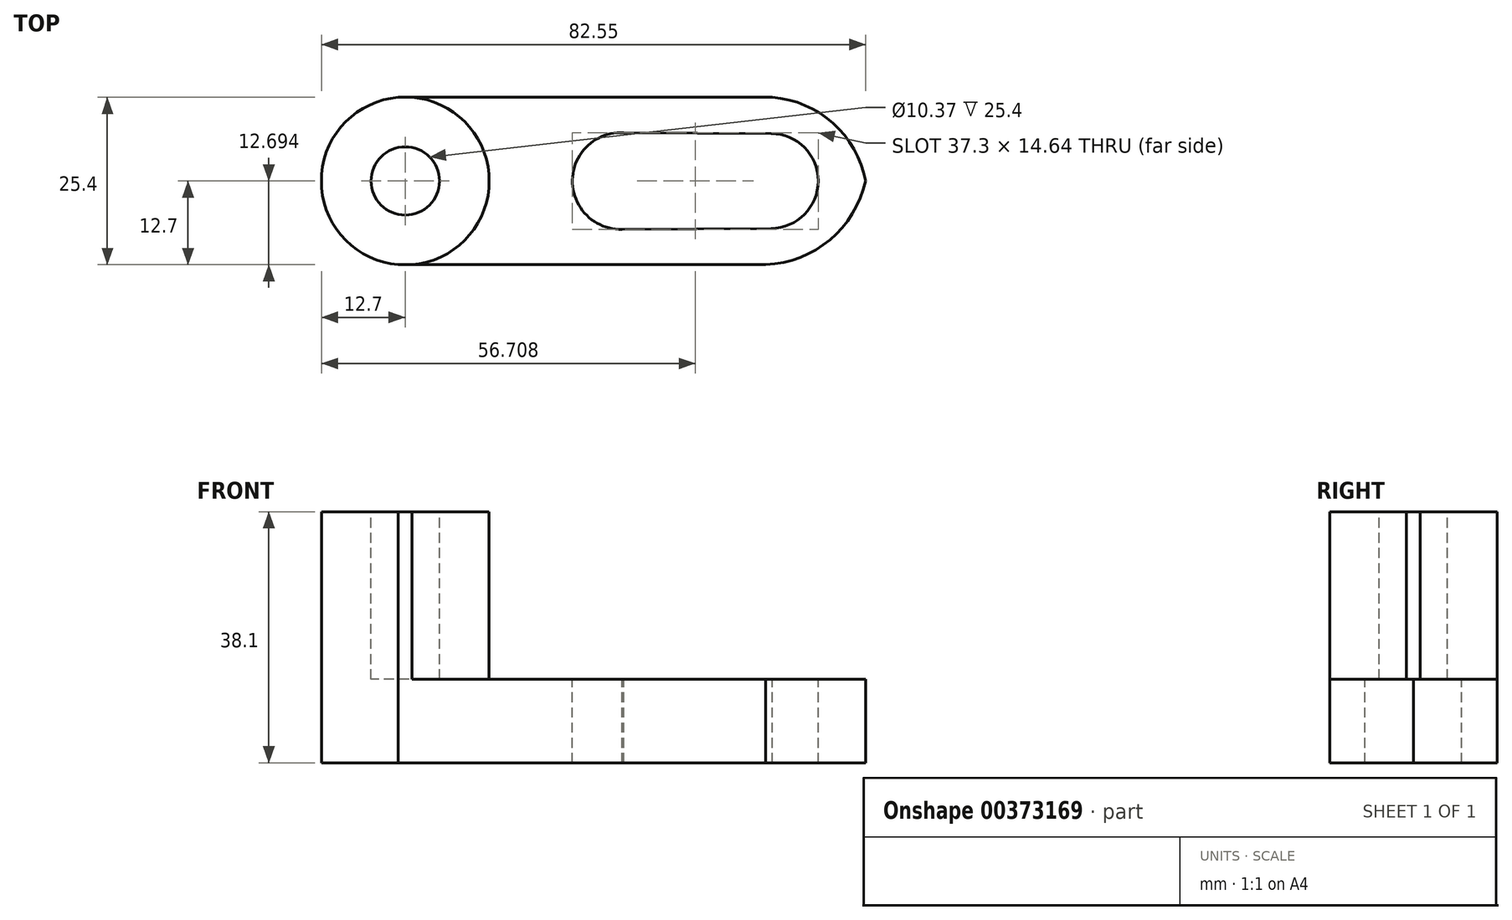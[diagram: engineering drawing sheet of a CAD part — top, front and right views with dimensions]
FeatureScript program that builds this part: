
annotation { "Feature Type Name" : "Feature", "Feature Type Description" : "" }
export const myFeature = defineFeature(function(context is Context, id is Id, definition is map)
    precondition{}
    {
        {
            var Q0;
            Q0=qCreatedBy(makeId("Front.planeOp"),FACE);
            var sketch = newSketch(context, id + "F0", { "sketchPlane" : qUnion([Q0])});
            skLineSegment(sketch, "E0", {"start": v(0, 0) * mm, "end": v(0, 38.1) * mm});
            skLineSegment(sketch, "E1", {"start": v(0, 38.1) * mm, "end": v(25.4, 38.1) * mm});
            skLineSegment(sketch, "E2", {"start": v(25.4, 38.1) * mm, "end": v(25.4, 12.7) * mm});
            skLineSegment(sketch, "E3", {"start": v(25.4, 12.7) * mm, "end": v(82.55, 12.7) * mm});
            skLineSegment(sketch, "E4", {"start": v(82.55, 12.7) * mm, "end": v(82.55, 0) * mm});
            skLineSegment(sketch, "E5", {"start": v(82.55, 0) * mm, "end": v(0, 0) * mm});
            skSolve(sketch);
        }
        {
            var Q0;
            Q0 = qSketchRegion(id + "F0", true);
            extrude(context, id + "F1", {"entities" : qUnion([Q0]), "depth" : 25.4 * mm});
        }
        {
            var Q0;
            Q0=makeQuery(id+"F1.opExtrude","SWEPT_FACE",FACE,{"disambiguationData":[OSD([sQuery(id+"F0.wireOp",EDGE,"E1")])]});
            var sketch = newSketch(context, id + "F2", { "sketchPlane" : qUnion([Q0])});
            skPoint(sketch, "E6.centerSnap0", {"position": v(12.7, 0) * mm});
            skPoint(sketch, "E6.centerSnap1", {"position": v(0, -12.7) * mm});
            skCircle(sketch, "E7", {"center": v(12.7, -12.7) * mm, "radius": 12.74 * mm});
            skCircle(sketch, "E8", {"center": v(12.7, -12.7) * mm, "radius": 5.18 * mm});
            skSolve(sketch);
        }
        {
            var Q0;
            Q0=makeQuery(id+"F2.imprint","IMPRINT",FACE,{"disambiguationData":[TD([[makeQuery(id+"F2.imprint","IMPRINT",EDGE,{"derivedFrom":sQuery(id+"F2.wireOp",EDGE,"E8")}),1.0]])]});
            var Q1;
            {var subQ0=sQuery(id+"F2.wireOp",EDGE,"E7");var subQ1=sQuery(id+"F0.wireOp",EDGE,"E1");var subQ2=makeQuery(id+"F1.opExtrude","CAP_EDGE",EDGE,{"disambiguationData":[OSD([subQ1])],"isStart":true});var subQ3=makeQuery(id+"F2.imprint","INTERSECT",VERTEX,{"disambiguationData":[OD(1.0)],"derivedFrom":[subQ2,subQ0]});Q1=makeQuery(id+"F2.imprint","IMPRINT",FACE,{"disambiguationData":[TD([[makeQuery(id+"F2.imprint","IMPRINT",EDGE,{"disambiguationData":[TD([[subQ3,-1.0]])],"derivedFrom":subQ0}),-1.0]])]});}
            var Q2;
            {var subQ0=sQuery(id+"F2.wireOp",EDGE,"E7");var subQ1=sQuery(id+"F0.wireOp",EDGE,"E1");var subQ2=makeQuery(id+"F1.opExtrude","CAP_EDGE",EDGE,{"disambiguationData":[OSD([subQ1])],"isStart":true});var subQ3=makeQuery(id+"F2.imprint","INTERSECT",VERTEX,{"disambiguationData":[OD(0.0)],"derivedFrom":[subQ2,subQ0]});Q2=makeQuery(id+"F2.imprint","IMPRINT",FACE,{"disambiguationData":[TD([[makeQuery(id+"F2.imprint","IMPRINT",EDGE,{"disambiguationData":[TD([[subQ3,1.0]])],"derivedFrom":subQ0}),-1.0]])]});}
            var Q3;
            {var subQ0=sQuery(id+"F2.wireOp",EDGE,"E7");var subQ1=sQuery(id+"F0.wireOp",EDGE,"E1");var subQ4=makeQuery(id+"F1.opExtrude","CAP_EDGE",EDGE,{"disambiguationData":[OSD([subQ1])],"isStart":false});var subQ5=makeQuery(id+"F2.imprint","INTERSECT",VERTEX,{"disambiguationData":[OD(0.0)],"derivedFrom":[subQ4,subQ0]});Q3=makeQuery(id+"F2.imprint","IMPRINT",FACE,{"disambiguationData":[TD([[makeQuery(id+"F2.imprint","IMPRINT",EDGE,{"disambiguationData":[TD([[subQ5,1.0]])],"derivedFrom":subQ0}),-1.0]])]});}
            var Q4;
            {var subQ0=sQuery(id+"F2.wireOp",EDGE,"E7");var subQ1=sQuery(id+"F0.wireOp",EDGE,"E1");var subQ2=makeQuery(id+"F1.opExtrude","CAP_EDGE",EDGE,{"disambiguationData":[OSD([subQ1])],"isStart":false});var subQ3=makeQuery(id+"F2.imprint","INTERSECT",VERTEX,{"disambiguationData":[OD(1.0)],"derivedFrom":[subQ2,subQ0]});Q4=makeQuery(id+"F2.imprint","IMPRINT",FACE,{"disambiguationData":[TD([[makeQuery(id+"F2.imprint","IMPRINT",EDGE,{"disambiguationData":[TD([[subQ3,-1.0]])],"derivedFrom":subQ0}),-1.0]])]});}
            extrude(context, id + "F3", {"entities" : qUnion([Q0, Q1, Q2, Q3, Q4]), "operationType" : NewBodyOperationType.REMOVE, "oppositeDirection" : true, "depth" : 25.4 * mm});
        }
        {
            var Q0;
            {var subQ0=sQuery(id+"F0.wireOp",EDGE,"E1");var subQ1=makeQuery(id+"F1.opExtrude","CAP_EDGE",EDGE,{"disambiguationData":[OSD([subQ0])],"isStart":false});var subQ2=sQuery(id+"F0.wireOp",EDGE,"E0");var subQ3=makeQuery(id+"F1.opExtrude","SWEPT_EDGE",EDGE,{"disambiguationData":[OSD([subQ2,subQ0])]});var subQ4=makeQuery(id+"F2.imprint","INTERSECT",VERTEX,{"derivedFrom":[subQ3,subQ1]});var subQ5=sQuery(id+"F2.wireOp",EDGE,"E7");var subQ6=makeQuery(id+"F2.imprint","INTERSECT",VERTEX,{"disambiguationData":[OD(0.0)],"derivedFrom":[subQ1,subQ5]});Q0=makeQuery(id+"F3.boolean.opBoolean","COPY",FACE,{"derivedFrom":makeQuery(id+"F3.opExtrude","CAP_FACE",FACE,{"disambiguationData":[OSD([subQ2,subQ0,subQ5]),TDD([makeQuery(id+"F2.imprint","IMPRINT",EDGE,{"disambiguationData":[TD([[subQ6,1.0]])],"derivedFrom":subQ5}),makeQuery(id+"F2.imprint","IMPRINT",EDGE,{"disambiguationData":[TD([[subQ4,-1.0]])],"derivedFrom":subQ3}),makeQuery(id+"F2.imprint","IMPRINT",EDGE,{"disambiguationData":[TD([[subQ6,1.0]])],"derivedFrom":subQ1})])],"isStart":false})});}
            var Q1;
            {var subQ0=sQuery(id+"F0.wireOp",EDGE,"E1");var subQ1=makeQuery(id+"F1.opExtrude","CAP_EDGE",EDGE,{"disambiguationData":[OSD([subQ0])],"isStart":true});var subQ2=sQuery(id+"F0.wireOp",EDGE,"E0");var subQ3=makeQuery(id+"F1.opExtrude","SWEPT_EDGE",EDGE,{"disambiguationData":[OSD([subQ2,subQ0])]});var subQ4=makeQuery(id+"F2.imprint","INTERSECT",VERTEX,{"derivedFrom":[subQ3,subQ1]});var subQ5=sQuery(id+"F2.wireOp",EDGE,"E7");var subQ6=makeQuery(id+"F2.imprint","INTERSECT",VERTEX,{"disambiguationData":[OD(1.0)],"derivedFrom":[subQ1,subQ5]});Q1=makeQuery(id+"F3.boolean.opBoolean","COPY",FACE,{"derivedFrom":makeQuery(id+"F3.opExtrude","CAP_FACE",FACE,{"disambiguationData":[OSD([subQ2,subQ0,subQ5]),TDD([makeQuery(id+"F2.imprint","IMPRINT",EDGE,{"disambiguationData":[TD([[subQ6,-1.0]])],"derivedFrom":subQ5}),makeQuery(id+"F2.imprint","IMPRINT",EDGE,{"disambiguationData":[TD([[subQ4,1.0]])],"derivedFrom":subQ3}),makeQuery(id+"F2.imprint","IMPRINT",EDGE,{"disambiguationData":[TD([[subQ6,1.0]])],"derivedFrom":subQ1})])],"isStart":false})});}
            extrude(context, id + "F4", {"entities" : qUnion([Q0, Q1]), "operationType" : NewBodyOperationType.REMOVE, "oppositeDirection" : true, "depth" : 12.7 * mm});
        }
        {
            var Q0;
            {var subQ0=sQuery(id+"F0.wireOp",EDGE,"E1");var subQ1=makeQuery(id+"F1.opExtrude","CAP_EDGE",EDGE,{"disambiguationData":[OSD([subQ0])],"isStart":false});var subQ2=sQuery(id+"F0.wireOp",EDGE,"E2");var subQ3=makeQuery(id+"F1.opExtrude","SWEPT_EDGE",EDGE,{"disambiguationData":[OSD([subQ0,subQ2])]});var subQ4=makeQuery(id+"F2.imprint","INTERSECT",VERTEX,{"derivedFrom":[subQ3,subQ1]});var subQ5=sQuery(id+"F2.wireOp",EDGE,"E7");var subQ6=makeQuery(id+"F2.imprint","INTERSECT",VERTEX,{"disambiguationData":[OD(1.0)],"derivedFrom":[subQ1,subQ5]});var subQ8=makeQuery(id+"F1.opExtrude","CAP_EDGE",EDGE,{"disambiguationData":[OSD([subQ0])],"isStart":true});var subQ9=makeQuery(id+"F2.imprint","INTERSECT",VERTEX,{"derivedFrom":[subQ3,subQ8]});var subQ10=makeQuery(id+"F2.imprint","INTERSECT",VERTEX,{"disambiguationData":[OD(0.0)],"derivedFrom":[subQ8,subQ5]});Q0=makeQuery(id+"F3.boolean.opBoolean","MERGE",FACE,{"derivedFrom":[makeQuery(id+"F1.opExtrude","SWEPT_FACE",FACE,{"disambiguationData":[OSD([sQuery(id+"F0.wireOp",EDGE,"E3")])]}),makeQuery(id+"F3.opExtrude","CAP_FACE",FACE,{"disambiguationData":[OSD([subQ0,subQ2,subQ5]),TDD([makeQuery(id+"F2.imprint","IMPRINT",EDGE,{"disambiguationData":[TD([[subQ10,1.0]])],"derivedFrom":subQ5}),makeQuery(id+"F2.imprint","IMPRINT",EDGE,{"disambiguationData":[TD([[subQ9,1.0]])],"derivedFrom":subQ3}),makeQuery(id+"F2.imprint","IMPRINT",EDGE,{"disambiguationData":[TD([[subQ10,-1.0]])],"derivedFrom":subQ8})])],"isStart":false}),makeQuery(id+"F3.opExtrude","CAP_FACE",FACE,{"disambiguationData":[OSD([subQ0,subQ2,subQ5]),TDD([makeQuery(id+"F2.imprint","IMPRINT",EDGE,{"disambiguationData":[TD([[subQ6,-1.0]])],"derivedFrom":subQ5}),makeQuery(id+"F2.imprint","IMPRINT",EDGE,{"disambiguationData":[TD([[subQ4,-1.0]])],"derivedFrom":subQ3}),makeQuery(id+"F2.imprint","IMPRINT",EDGE,{"disambiguationData":[TD([[subQ6,-1.0]])],"derivedFrom":subQ1})])],"isStart":false})]});}
            var sketch = newSketch(context, id + "F5", { "sketchPlane" : qUnion([Q0])});
            skArc(sketch, "E9", {"start": v(82.55, -12.7) * mm, "mid": v(76.72, -3.2) * mm, "end": v(66.03, 0) * mm});
            skArc(sketch, "E10", {"start": v(66.03, -25.4) * mm, "mid": v(76.6, -22.05) * mm, "end": v(82.55, -12.7) * mm});
            skCircle(sketch, "E11", {"center": v(68.17, -12.7) * mm, "radius": 7.2 * mm});
            skCircle(sketch, "E12", {"center": v(45.38, -12.7) * mm, "radius": 7.33 * mm});
            skLineSegment(sketch, "E13", {"start": v(44.99, -5.38) * mm, "end": v(68.2, -5.5) * mm});
            skLineSegment(sketch, "E14", {"start": v(45.26, -20.03) * mm, "end": v(68.2, -19.9) * mm});
            skSolve(sketch);
        }
        {
            var Q0;
            Q0 = qSketchRegion(id + "F5", true);
            var Q1;
            {var subQ0=sQuery(id+"F5.wireOp",EDGE,"E9");var subQ1=sQuery(id+"F0.wireOp",EDGE,"E3");var subQ2=makeQuery(id+"F1.opExtrude","SWEPT_EDGE",EDGE,{"disambiguationData":[OSD([subQ1,sQuery(id+"F0.wireOp",EDGE,"E4")])]});var subQ3=makeQuery(id+"F5.imprint","INTERSECT",VERTEX,{"derivedFrom":[subQ2,subQ0,sQuery(id+"F5.wireOp",EDGE,"E10")]});Q1=makeQuery(id+"F5.imprint","IMPRINT",FACE,{"disambiguationData":[TD([[makeQuery(id+"F5.imprint","IMPRINT",EDGE,{"disambiguationData":[TD([[subQ3,-1.0]])],"derivedFrom":subQ0}),-1.0]])]});}
            var Q2;
            {var subQ0=sQuery(id+"F5.wireOp",EDGE,"E10");var subQ1=sQuery(id+"F0.wireOp",EDGE,"E3");var subQ2=makeQuery(id+"F1.opExtrude","SWEPT_EDGE",EDGE,{"disambiguationData":[OSD([subQ1,sQuery(id+"F0.wireOp",EDGE,"E4")])]});var subQ3=makeQuery(id+"F5.imprint","INTERSECT",VERTEX,{"derivedFrom":[subQ2,sQuery(id+"F5.wireOp",EDGE,"E9"),subQ0]});Q2=makeQuery(id+"F5.imprint","IMPRINT",FACE,{"disambiguationData":[TD([[makeQuery(id+"F5.imprint","IMPRINT",EDGE,{"disambiguationData":[TD([[subQ3,1.0]])],"derivedFrom":subQ0}),-1.0]])]});}
            extrude(context, id + "F6", {"entities" : qUnion([Q0, Q1, Q2]), "operationType" : NewBodyOperationType.REMOVE, "oppositeDirection" : true, "depth" : 12.7 * mm});
        }
    });
